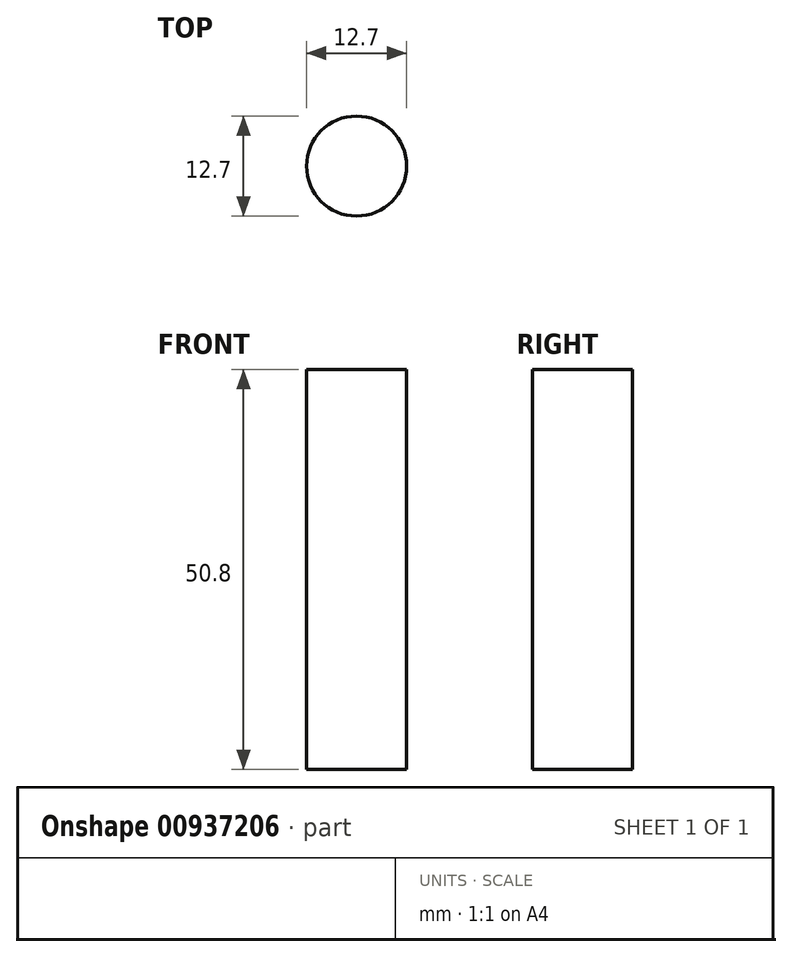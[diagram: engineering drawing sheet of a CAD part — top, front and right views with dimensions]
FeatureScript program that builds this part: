
annotation { "Feature Type Name" : "Feature", "Feature Type Description" : "" }
export const myFeature = defineFeature(function(context is Context, id is Id, definition is map)
    precondition{}
    {
        {
            var Q0;
            Q0=qCreatedBy(makeId("Top.planeOp"),FACE);
            var sketch = newSketch(context, id + "F0", { "sketchPlane" : qUnion([Q0])});
            skCircle(sketch, "E0", {"center": v(-16.74, 15.54) * mm, "radius": 6.35 * mm});
            skSolve(sketch);
        }
        {
            var Q0;
            Q0 = qSketchRegion(id + "F0", true);
            extrude(context, id + "F1", {"entities" : qUnion([Q0]), "depth" : 50.8 * mm, "offsetDistance" : 25.4 * mm});
        }
    });
